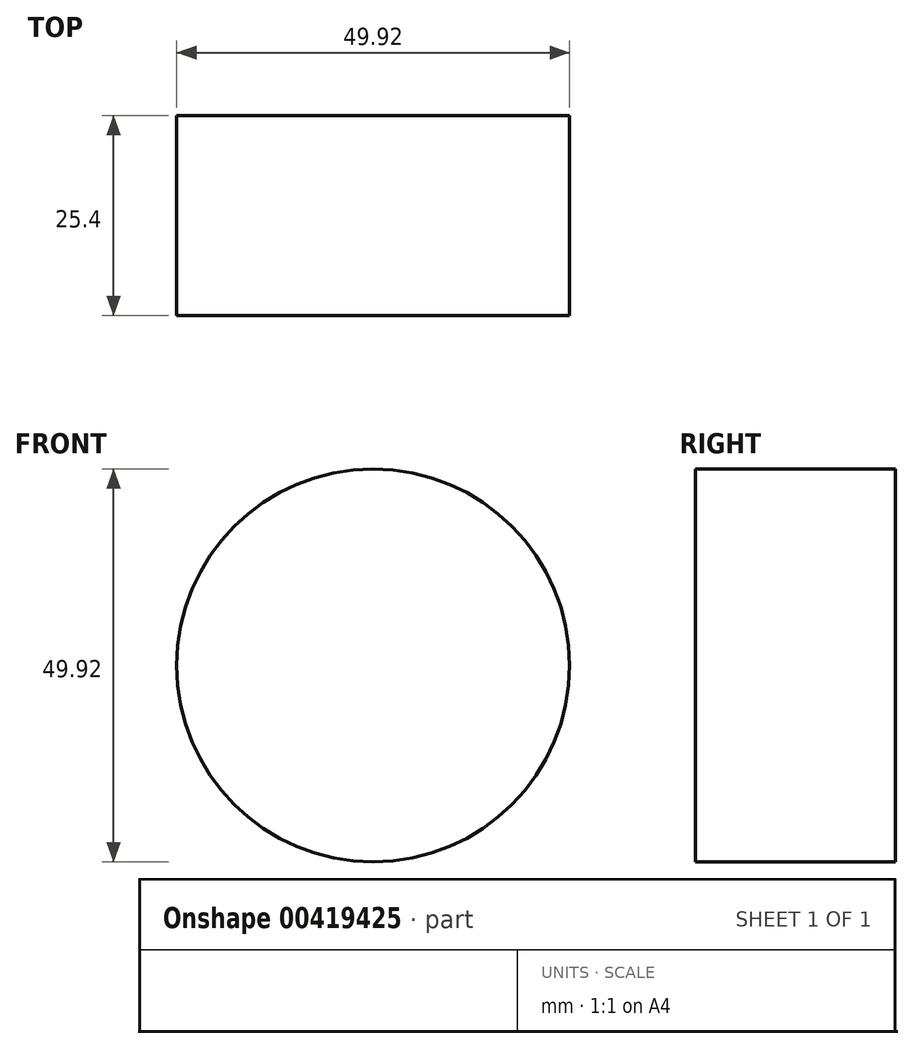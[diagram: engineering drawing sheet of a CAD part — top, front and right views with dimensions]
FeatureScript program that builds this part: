
annotation { "Feature Type Name" : "Feature", "Feature Type Description" : "" }
export const myFeature = defineFeature(function(context is Context, id is Id, definition is map)
    precondition{}
    {
        {
            var Q0;
            Q0=qCreatedBy(makeId("Front.planeOp"),FACE);
            var sketch = newSketch(context, id + "F0", { "sketchPlane" : qUnion([Q0])});
            skCircle(sketch, "E0", {"center": v(0, 0) * mm, "radius": 24.96 * mm});
            skSolve(sketch);
        }
        {
            var Q0;
            Q0 = qSketchRegion(id + "F0", true);
            extrude(context, id + "F1", {"entities" : qUnion([Q0]), "depth" : 25.4 * mm});
        }
    });
